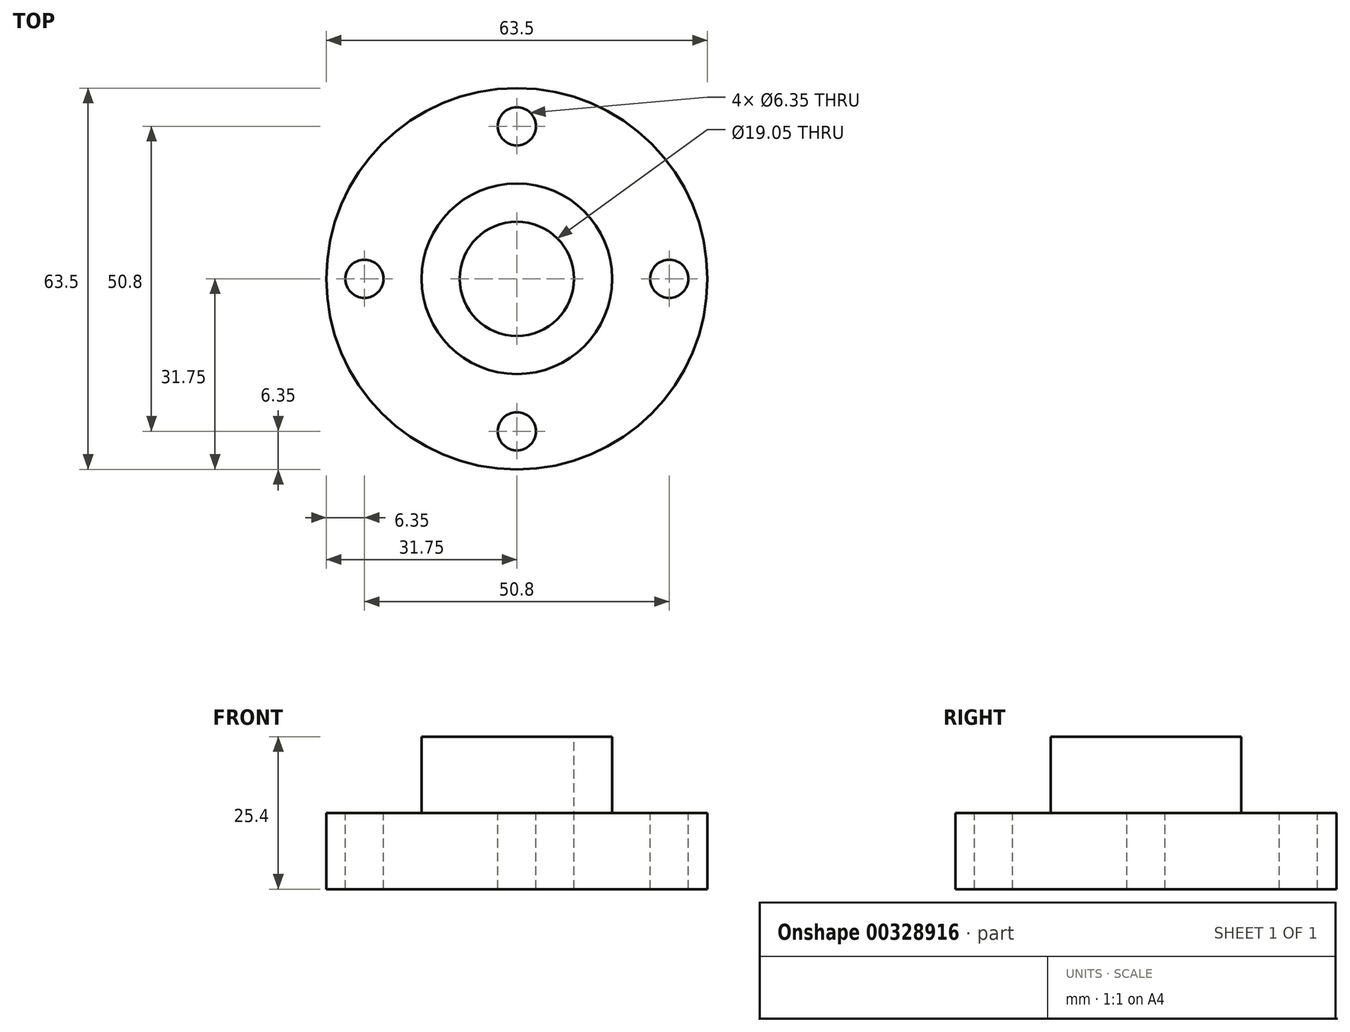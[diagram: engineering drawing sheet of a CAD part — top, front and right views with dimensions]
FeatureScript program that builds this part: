
annotation { "Feature Type Name" : "Feature", "Feature Type Description" : "" }
export const myFeature = defineFeature(function(context is Context, id is Id, definition is map)
    precondition{}
    {
        {
            var Q0;
            Q0=qCreatedBy(makeId("Top.planeOp"),FACE);
            var sketch = newSketch(context, id + "F0", { "sketchPlane" : qUnion([Q0])});
            skCircle(sketch, "E0", {"center": v(0, 0) * mm, "radius": 31.75 * mm});
            skCircle(sketch, "E1", {"center": v(0, 0) * mm, "radius": 15.88 * mm});
            skSolve(sketch);
        }
        {
            var Q0;
            Q0 = qSketchRegion(id + "F0", true);
            var Q1;
            Q1=makeQuery(id+"F0.imprint","IMPRINT",FACE,{"disambiguationData":[TD([[makeQuery(id+"F0.imprint","IMPRINT",EDGE,{"derivedFrom":sQuery(id+"F0.wireOp",EDGE,"E1")}),1.0]])]});
            extrude(context, id + "F1", {"entities" : qUnion([Q0, Q1]), "depth" : 12.7 * mm});
        }
        {
            var Q0;
            Q0=makeQuery(id+"F1.opExtrude","CAP_FACE",FACE,{"disambiguationData":[OSD([sQuery(id+"F0.wireOp",EDGE,"E0")])],"isStart":false});
            var sketch = newSketch(context, id + "F2", { "sketchPlane" : qUnion([Q0])});
            skCircle(sketch, "E2", {"center": v(0, 0) * mm, "radius": 15.88 * mm});
            skSolve(sketch);
        }
        {
            var Q0;
            Q0 = qSketchRegion(id + "F2", true);
            extrude(context, id + "F3", {"entities" : qUnion([Q0]), "operationType" : NewBodyOperationType.ADD, "depth" : 12.7 * mm});
        }
        {
            var Q0;
            Q0=makeQuery(id+"F3.opExtrude","CAP_FACE",FACE,{"disambiguationData":[OSD([sQuery(id+"F2.wireOp",EDGE,"E2")])],"isStart":false});
            var sketch = newSketch(context, id + "F4", { "sketchPlane" : qUnion([Q0])});
            skCircle(sketch, "E3", {"center": v(0, 0) * mm, "radius": 9.53 * mm});
            skSolve(sketch);
        }
        {
            var Q0;
            Q0 = qSketchRegion(id + "F4", true);
            var Q1;
            Q1=makeQuery(id+"F1.opExtrude","CAP_FACE",FACE,{"disambiguationData":[OSD([sQuery(id+"F0.wireOp",EDGE,"E0")])],"isStart":true});
            extrude(context, id + "F5", {"entities" : qUnion([Q0]), "operationType" : NewBodyOperationType.REMOVE, "endBound" : BoundingType.UP_TO_SURFACE, "oppositeDirection" : true, "endBoundEntityFace" : qUnion([Q1]), "depth" : 25.4 * mm});
        }
        {
            var Q0;
            Q0=makeQuery(id+"F1.opExtrude","CAP_FACE",FACE,{"disambiguationData":[OSD([sQuery(id+"F0.wireOp",EDGE,"E0")])],"isStart":false});
            var sketch = newSketch(context, id + "F6", { "sketchPlane" : qUnion([Q0])});
            skCircle(sketch, "E4", {"center": v(0, 25.4) * mm, "radius": 3.18 * mm});
            skCircle(sketch, "E5", {"center": v(0, -25.4) * mm, "radius": 3.18 * mm});
            skCircle(sketch, "E6", {"center": v(25.4, 0) * mm, "radius": 3.18 * mm});
            skCircle(sketch, "E7", {"center": v(-25.4, 0) * mm, "radius": 3.18 * mm});
            skSolve(sketch);
        }
        {
            var Q0;
            Q0 = qSketchRegion(id + "F6", true);
            var Q1;
            Q1=makeQuery(id+"F1.opExtrude","CAP_FACE",FACE,{"disambiguationData":[OSD([sQuery(id+"F0.wireOp",EDGE,"E0")])],"isStart":true});
            extrude(context, id + "F7", {"entities" : qUnion([Q0]), "operationType" : NewBodyOperationType.REMOVE, "endBound" : BoundingType.UP_TO_SURFACE, "oppositeDirection" : true, "endBoundEntityFace" : qUnion([Q1]), "depth" : 25.4 * mm});
        }
    });
